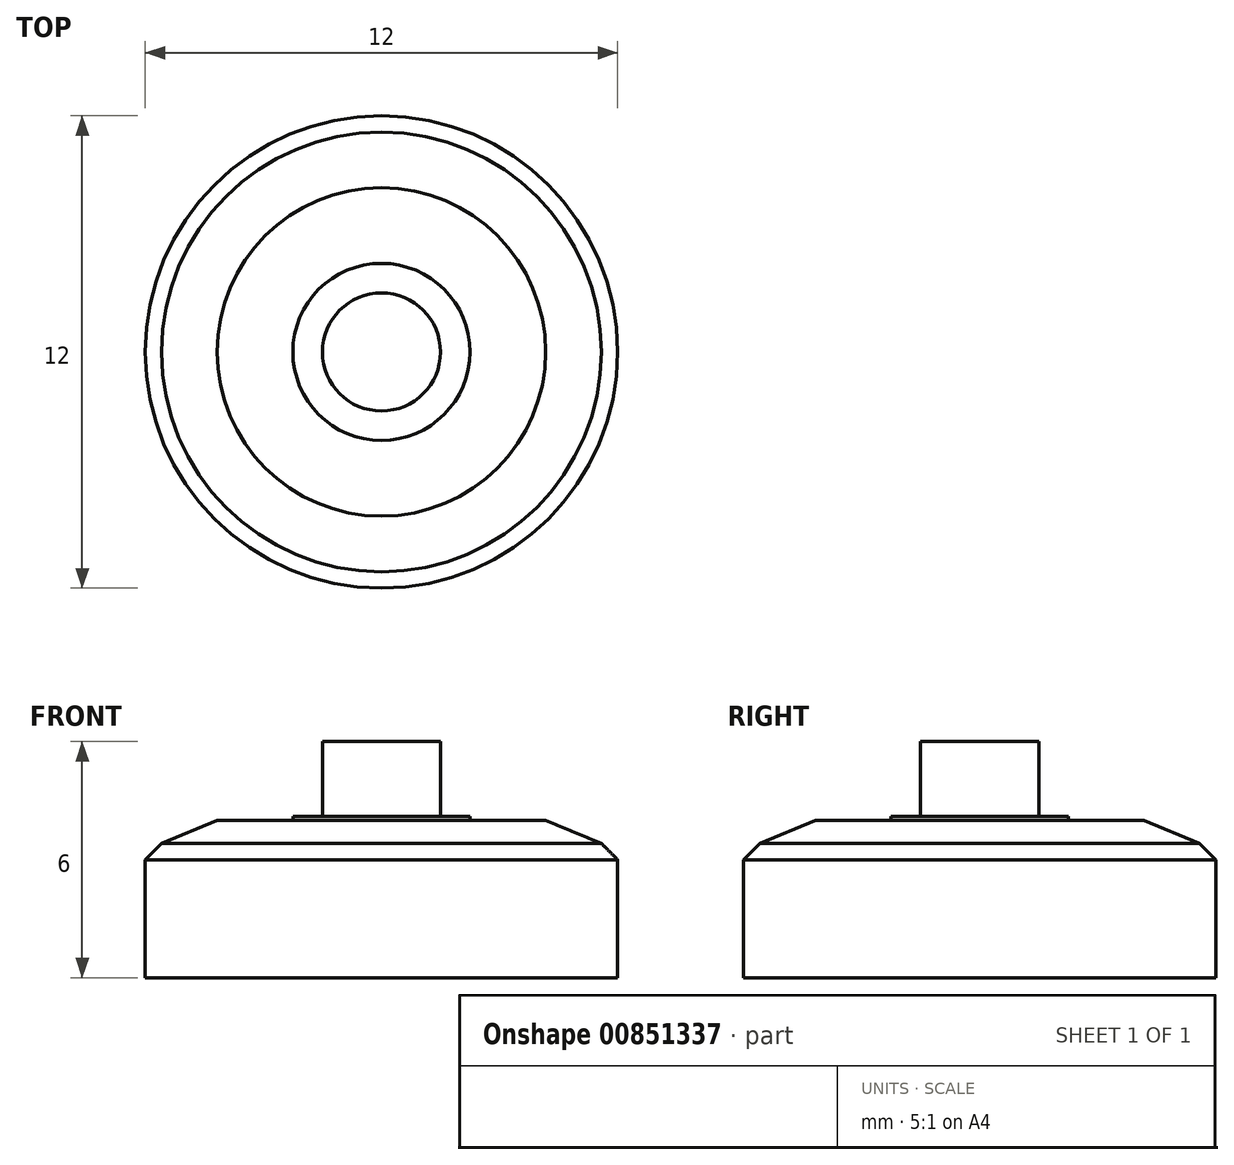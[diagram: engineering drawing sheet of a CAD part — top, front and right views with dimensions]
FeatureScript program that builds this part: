
annotation { "Feature Type Name" : "Feature", "Feature Type Description" : "" }
export const myFeature = defineFeature(function(context is Context, id is Id, definition is map)
    precondition{}
    {
        {
            var Q0;
            Q0=qCreatedBy(makeId("Top.planeOp"),FACE);
            var sketch = newSketch(context, id + "F0", { "sketchPlane" : qUnion([Q0])});
            skCircle(sketch, "E0", {"center": v(0, 0) * mm, "radius": 6 * mm});
            skCircle(sketch, "E1", {"center": v(0, 0) * mm, "radius": 1.5 * mm});
            skCircle(sketch, "E2", {"center": v(0, 0) * mm, "radius": 2.25 * mm});
            skSolve(sketch);
        }
        {
            var Q0;
            Q0=makeQuery(id+"F0.imprint","IMPRINT",FACE,{"disambiguationData":[TD([[makeQuery(id+"F0.imprint","IMPRINT",EDGE,{"derivedFrom":sQuery(id+"F0.wireOp",EDGE,"E1")}),1.0]])]});
            extrude(context, id + "F1", {"entities" : qUnion([Q0]), "depth" : 6 * mm, "offsetDistance" : 25 * mm});
        }
        {
            var Q0;
            Q0=makeQuery(id+"F0.imprint","IMPRINT",FACE,{"disambiguationData":[TD([[makeQuery(id+"F0.imprint","IMPRINT",EDGE,{"derivedFrom":sQuery(id+"F0.wireOp",EDGE,"E1")}),-1.0]])]});
            extrude(context, id + "F2", {"entities" : qUnion([Q0]), "operationType" : NewBodyOperationType.ADD, "depth" : 4.1 * mm, "offsetDistance" : 25 * mm});
        }
        {
            var Q0;
            Q0=makeQuery(id+"F0.imprint","IMPRINT",FACE,{"disambiguationData":[TD([[makeQuery(id+"F0.imprint","IMPRINT",EDGE,{"derivedFrom":sQuery(id+"F0.wireOp",EDGE,"E0")}),1.0]])]});
            extrude(context, id + "F3", {"entities" : qUnion([Q0]), "operationType" : NewBodyOperationType.ADD, "depth" : 4 * mm, "offsetDistance" : 25 * mm});
        }
        {
            var Q0;
            Q0=makeQuery(id+"F3.opExtrude","CAP_EDGE",EDGE,{"disambiguationData":[OSD([sQuery(id+"F0.wireOp",EDGE,"E0")])],"isStart":false});
            chamfer(context, id + "F4", {"entities" : qUnion([Q0]), "width" : 1 * mm, "tangentPropagation" : true});
        }
        {
            var Q0;
            {var subQ0=sQuery(id+"F0.wireOp",EDGE,"E0");Q0=makeQuery(id+"F4.opChamfer","BLEND_EDGE",EDGE,{"blendedFrom":[makeQuery(id+"F3.opExtrude","CAP_EDGE",EDGE,{"disambiguationData":[OSD([subQ0])],"isStart":false}),makeQuery(id+"F3.opExtrude","CAP_FACE",FACE,{"disambiguationData":[OSD([subQ0,sQuery(id+"F0.wireOp",EDGE,"E2")])],"isStart":false})],"blendedInto":[makeQuery(id+"F3.opExtrude","CAP_FACE",FACE,{"disambiguationData":[OSD([subQ0,sQuery(id+"F0.wireOp",EDGE,"E2")])],"isStart":false})]});}
            chamfer(context, id + "F5", {"entities" : qUnion([Q0]), "width" : 2 * mm, "tangentPropagation" : true});
        }
    });
